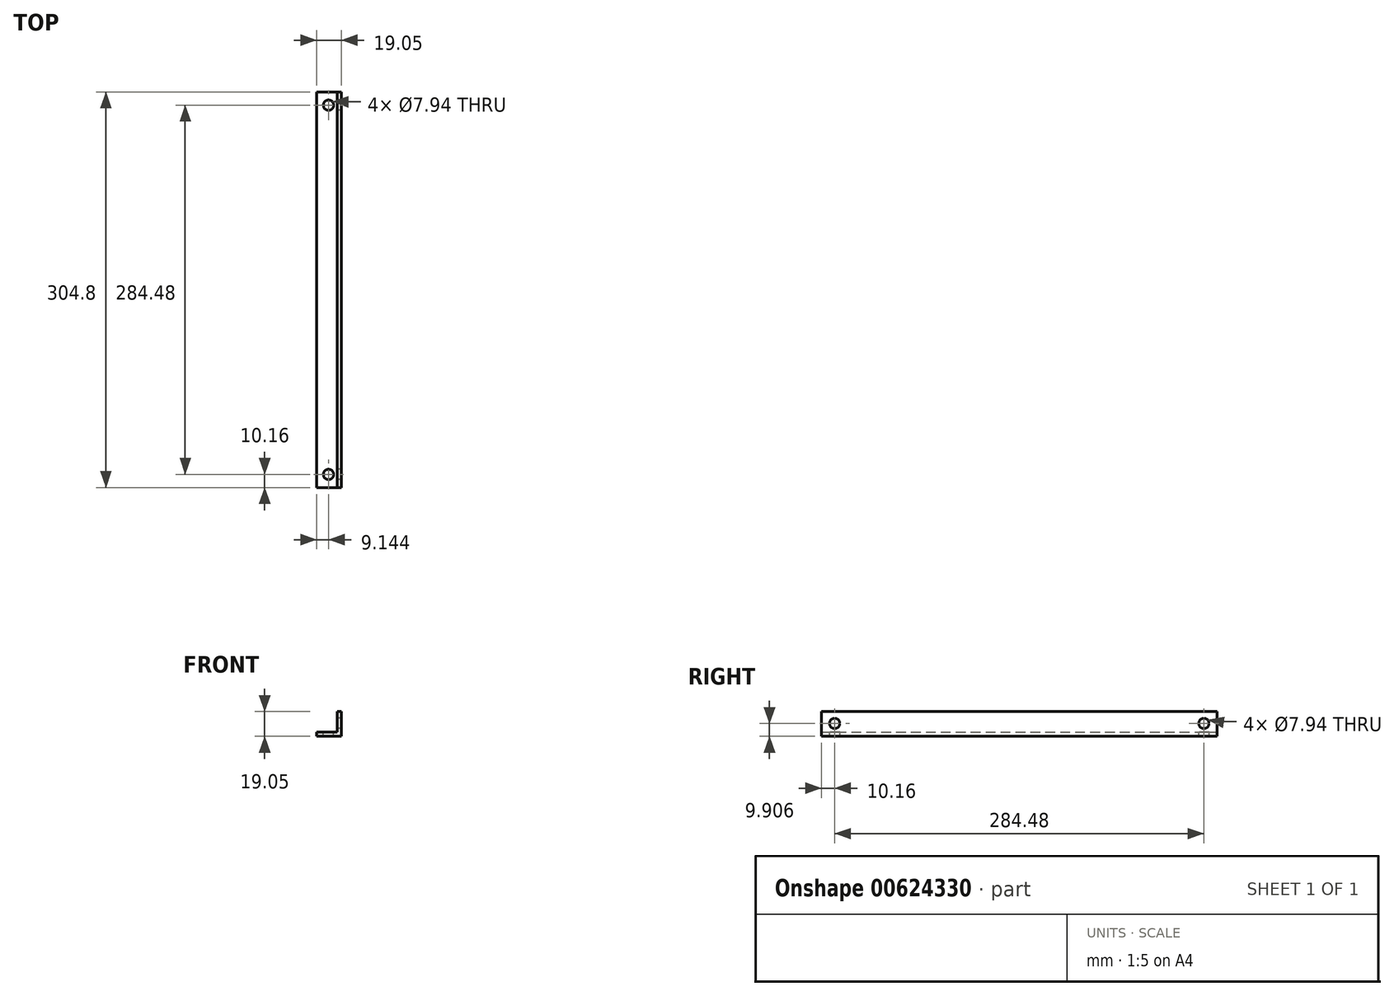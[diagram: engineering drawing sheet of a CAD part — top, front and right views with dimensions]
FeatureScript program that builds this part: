
annotation { "Feature Type Name" : "Feature", "Feature Type Description" : "" }
export const myFeature = defineFeature(function(context is Context, id is Id, definition is map)
    precondition{}
    {
        {
            var Q0;
            Q0=qCreatedBy(makeId("Front.planeOp"),FACE);
            var sketch = newSketch(context, id + "F0", { "sketchPlane" : qUnion([Q0])});
            skLineSegment(sketch, "E0", {"start": v(0, 0) * mm, "end": v(0, 19.05) * mm});
            skLineSegment(sketch, "E1", {"start": v(0, 19.05) * mm, "end": v(-3.25, 19.05) * mm});
            skLineSegment(sketch, "E2", {"start": v(-3.25, 19.05) * mm, "end": v(-3.25, 3.25) * mm});
            skLineSegment(sketch, "E3", {"start": v(-3.25, 3.25) * mm, "end": v(-19.05, 3.25) * mm});
            skLineSegment(sketch, "E4", {"start": v(-19.05, 3.25) * mm, "end": v(-19.05, 0) * mm});
            skLineSegment(sketch, "E5", {"start": v(-19.05, 0) * mm, "end": v(0, 0) * mm});
            skSolve(sketch);
        }
        {
            var Q0;
            Q0=makeQuery(id+"F0.imprint","IMPRINT",FACE,{"disambiguationData":[TD([[makeQuery(id+"F0.imprint","IMPRINT",EDGE,{"derivedFrom":sQuery(id+"F0.wireOp",EDGE,"E0")}),1.0]])]});
            extrude(context, id + "F1", {"entities" : qUnion([Q0]), "endBound" : BoundingType.SYMMETRIC, "depth" : 304.8 * mm, "offsetDistance" : 25.4 * mm});
        }
        {
            var Q0;
            Q0=makeQuery(id+"F1.opExtrude","SWEPT_FACE",FACE,{"disambiguationData":[OSD([sQuery(id+"F0.wireOp",EDGE,"E3")])]});
            var sketch = newSketch(context, id + "F2", { "sketchPlane" : qUnion([Q0])});
            skPoint(sketch, "E6", {"position": v(-9.9, -142.24) * mm});
            skLineSegment(sketch, "E7", {"start": v(-9.9, -152.4) * mm, "end": v(-9.9, 152.4) * mm, "construction": true});
            skPoint(sketch, "E8", {"position": v(-9.9, 142.24) * mm});
            skSolve(sketch);
        }
        {
            var Q0;
            Q0=sQuery(id+"F2.wireOp",VERTEX,"E6");
            var Q1;
            Q1=sQuery(id+"F2.wireOp",VERTEX,"E8");
            var Q2;
            Q2=makeQuery(id+"F1.opExtrude","SWEPT_BODY",BODY,{"disambiguationData":[OSD([sQuery(id+"F0.wireOp",EDGE,"E0"),sQuery(id+"F0.wireOp",EDGE,"E1"),sQuery(id+"F0.wireOp",EDGE,"E2"),sQuery(id+"F0.wireOp",EDGE,"E3"),sQuery(id+"F0.wireOp",EDGE,"E4"),sQuery(id+"F0.wireOp",EDGE,"E5")])]});
            hole(context, id + "F3", {"style" : HoleStyle.SIMPLE, "endStyle" : HoleEndStyle.BLIND, "standardTappedOrClearance" : lookupTablePath({ "standard" : "ANSI", "engagement" : "75%", "pitch" : "16 tpi", "size" : "3/8", "type" : "Tapped" }), "standardBlindInLast" : lookupTablePath({ "standard" : "ANSI", "engagement" : "75%", "pitch" : "16 tpi", "size" : "3/8", "type" : "Tapped" }), "holeDiameter" : 7.94 * mm, "majorDiameter" : 9.52 * mm, "showTappedDepth" : true, "holeDepth" : 17.46 * mm, "isTappedThrough" : true, "tappedDepth" : 12.7 * mm, "tapClearance" : 3, "startFromSketch" : true, "locations" : qUnion([Q0, Q1]), "scope" : qUnion([Q2])});
        }
        {
            var Q0;
            Q0=makeQuery(id+"F1.opExtrude","SWEPT_FACE",FACE,{"disambiguationData":[OSD([sQuery(id+"F0.wireOp",EDGE,"E2")])]});
            var sketch = newSketch(context, id + "F4", { "sketchPlane" : qUnion([Q0])});
            skLineSegment(sketch, "E9", {"start": v(152.4, 9.9) * mm, "end": v(-152.4, 9.9) * mm, "construction": true});
            skPoint(sketch, "E10", {"position": v(-142.24, 9.9) * mm});
            skPoint(sketch, "E11", {"position": v(142.24, 9.9) * mm});
            skSolve(sketch);
        }
        {
            var Q0;
            Q0=sQuery(id+"F4.wireOp",VERTEX,"E10");
            var Q1;
            Q1=sQuery(id+"F4.wireOp",VERTEX,"E11");
            var Q2;
            Q2=makeQuery(id+"F1.opExtrude","SWEPT_BODY",BODY,{"disambiguationData":[OSD([sQuery(id+"F0.wireOp",EDGE,"E0"),sQuery(id+"F0.wireOp",EDGE,"E1"),sQuery(id+"F0.wireOp",EDGE,"E2"),sQuery(id+"F0.wireOp",EDGE,"E3"),sQuery(id+"F0.wireOp",EDGE,"E4"),sQuery(id+"F0.wireOp",EDGE,"E5")])]});
            hole(context, id + "F5", {"style" : HoleStyle.SIMPLE, "endStyle" : HoleEndStyle.BLIND, "standardTappedOrClearance" : lookupTablePath({ "standard" : "ANSI", "engagement" : "75%", "pitch" : "16 tpi", "size" : "3/8", "type" : "Tapped" }), "standardBlindInLast" : lookupTablePath({ "standard" : "ANSI", "engagement" : "75%", "pitch" : "16 tpi", "size" : "3/8", "type" : "Tapped" }), "holeDiameter" : 7.94 * mm, "majorDiameter" : 9.52 * mm, "showTappedDepth" : true, "holeDepth" : 17.48 * mm, "isTappedThrough" : true, "tappedDepth" : 12.71 * mm, "tapClearance" : 3, "startFromSketch" : true, "locations" : qUnion([Q0, Q1]), "scope" : qUnion([Q2])});
        }
        {
            var Q0;
            Q0=makeQuery(id+"F1.opExtrude","SWEPT_EDGE",EDGE,{"disambiguationData":[OSD([sQuery(id+"F0.wireOp",EDGE,"E1"),sQuery(id+"F0.wireOp",EDGE,"E2")])]});
            var Q1;
            Q1=makeQuery(id+"F1.opExtrude","SWEPT_EDGE",EDGE,{"disambiguationData":[OSD([sQuery(id+"F0.wireOp",EDGE,"E3"),sQuery(id+"F0.wireOp",EDGE,"E4")])]});
            cPlane(context, id + "F6", {"entities" : qUnion([Q0, Q1]), "cplaneType" : CPlaneType.LINE_ANGLE, "offset" : 25.4 * mm, "angle" : 0 * degree, "width" : 152.4 * mm, "height" : 152.4 * mm});
        }
        {
            var Q0;
            Q0=qCreatedBy(id+"F6.planeOp",FACE);
            var sketch = newSketch(context, id + "F7", { "sketchPlane" : qUnion([Q0])});
            skPoint(sketch, "E12", {"position": v(0, 0) * mm});
            skSolve(sketch);
        }
    });
